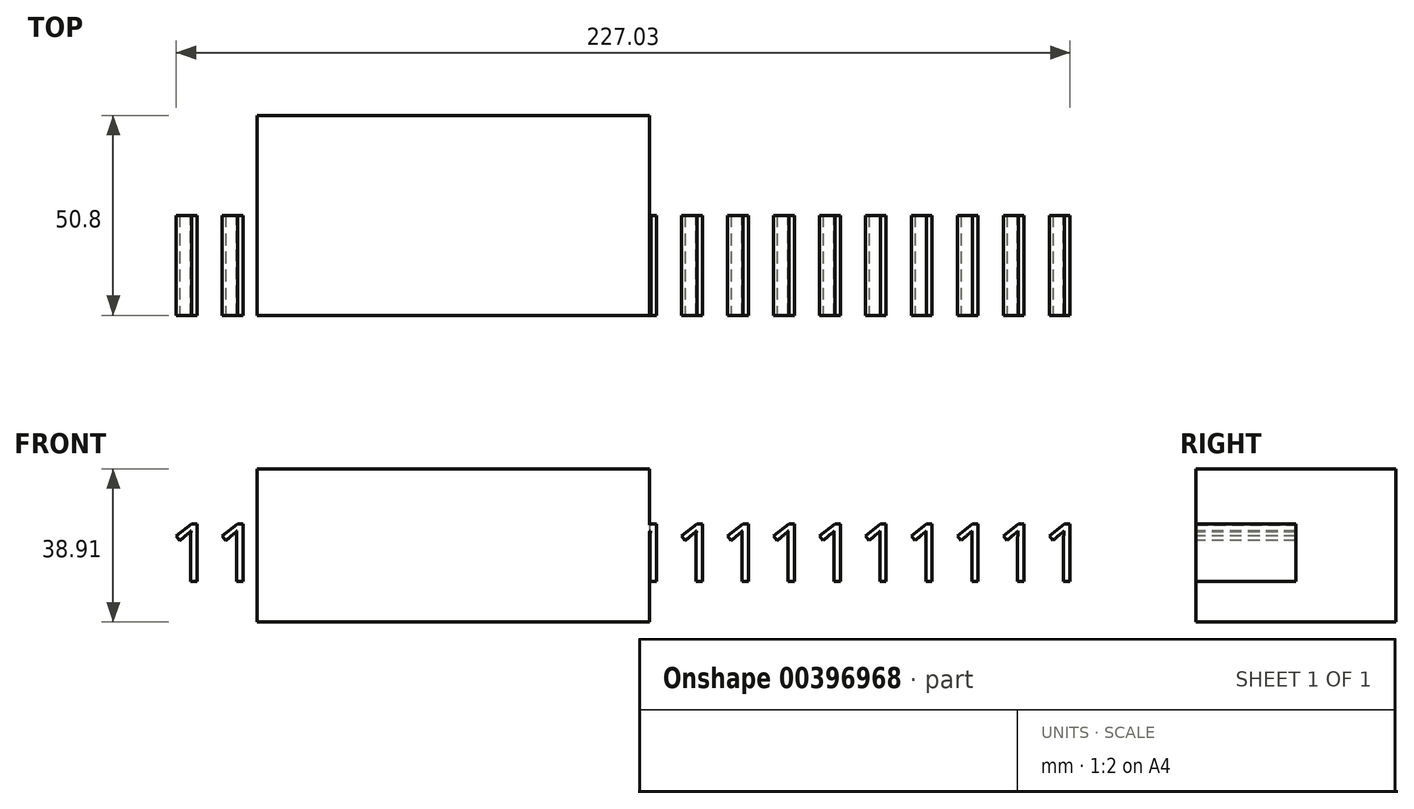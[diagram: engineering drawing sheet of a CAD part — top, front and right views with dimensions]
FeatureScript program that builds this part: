
annotation { "Feature Type Name" : "Feature", "Feature Type Description" : "" }
export const myFeature = defineFeature(function(context is Context, id is Id, definition is map)
    precondition{}
    {
        {
            var Q0;
            Q0=qCreatedBy(makeId("Front.planeOp"),FACE);
            var sketch = newSketch(context, id + "F0", { "sketchPlane" : qUnion([Q0])});
            skLineSegment(sketch, "E0.bottom", {"start": v(-78.4, 54.74) * mm, "end": v(21.3, 54.74) * mm});
            skLineSegment(sketch, "E0.top", {"start": v(-78.4, 15.83) * mm, "end": v(21.3, 15.83) * mm});
            skLineSegment(sketch, "E0.left", {"start": v(-78.4, 54.74) * mm, "end": v(-78.4, 15.83) * mm});
            skLineSegment(sketch, "E0.right", {"start": v(21.3, 54.74) * mm, "end": v(21.3, 15.83) * mm});
            skSolve(sketch);
        }
        {
            var Q0;
            Q0 = qSketchRegion(id + "F0", true);
            extrude(context, id + "F1", {"entities" : qUnion([Q0]), "depth" : 50.8 * mm});
        }
        {
            var Q0;
            Q0=makeQuery(id+"F1.opExtrude","CAP_FACE",FACE,{"disambiguationData":[OSD([sQuery(id+"F0.wireOp",EDGE,"E0.bottom"),sQuery(id+"F0.wireOp",EDGE,"E0.top"),sQuery(id+"F0.wireOp",EDGE,"E0.left"),sQuery(id+"F0.wireOp",EDGE,"E0.right")])],"isStart":false});
            var sketch = newSketch(context, id + "F2", { "sketchPlane" : qUnion([Q0])});
            skText(sketch, "E1", { "text": "11111111111111111111\n", "fontName": "OpenSans-Regular.ttf"});
            const initialGuessF2  = {"E1": [-0.10082, 0.02612, 1, 0, 0.0147]};
            skSetInitialGuess(sketch, initialGuessF2);
            skSolve(sketch);
        }
        {
            var Q0;
            Q0 = qSketchRegion(id + "F2", true);
            extrude(context, id + "F3", {"entities" : qUnion([Q0]), "operationType" : NewBodyOperationType.ADD, "depth" : -25.4 * mm});
        }
    });
